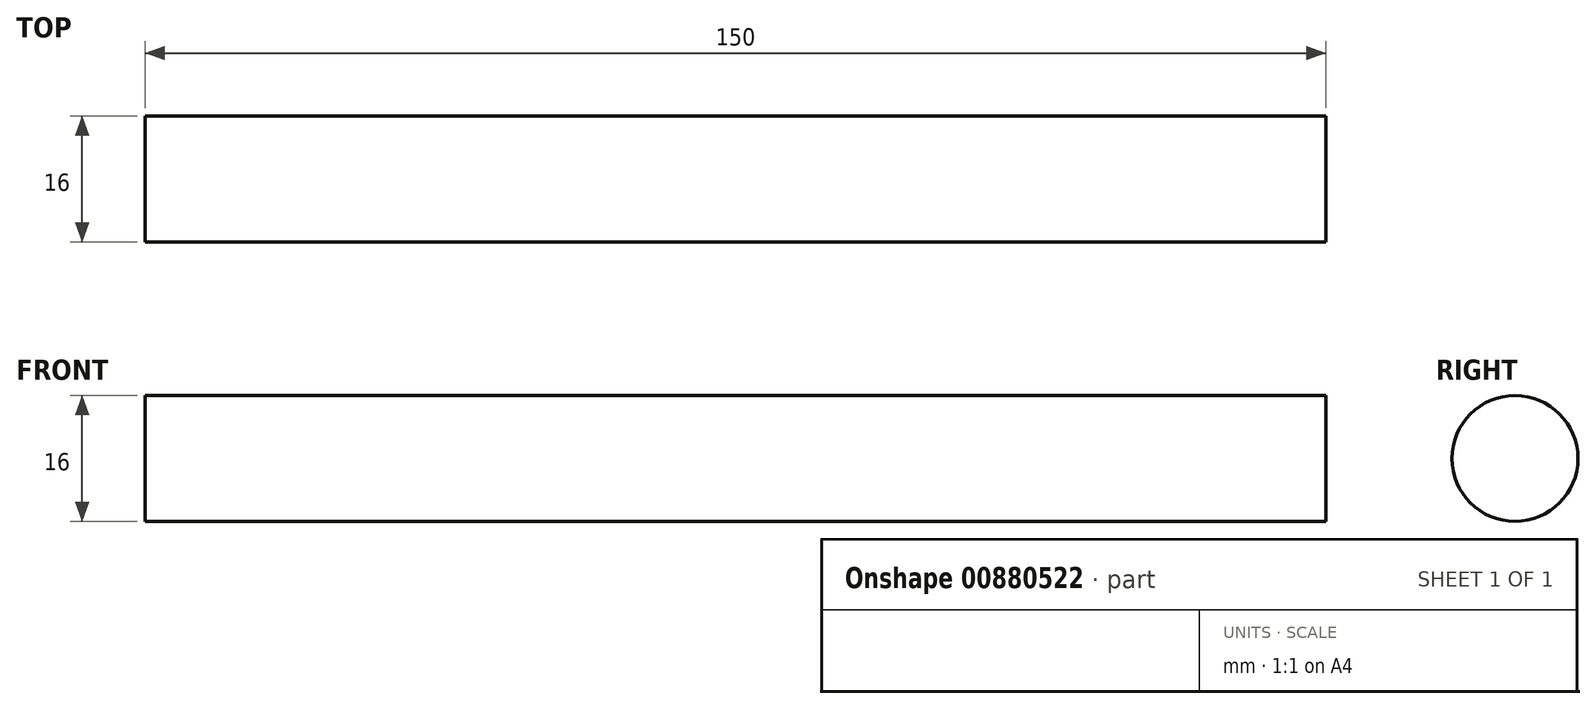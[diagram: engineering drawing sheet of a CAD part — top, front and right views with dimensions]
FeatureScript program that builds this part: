
annotation { "Feature Type Name" : "Feature", "Feature Type Description" : "" }
export const myFeature = defineFeature(function(context is Context, id is Id, definition is map)
    precondition{}
    {
        {
            var Q0;
            Q0=qCreatedBy(makeId("Right.planeOp"),FACE);
            var sketch = newSketch(context, id + "F0", { "sketchPlane" : qUnion([Q0])});
            skCircle(sketch, "E0", {"center": v(0, 0) * mm, "radius": 8 * mm});
            skSolve(sketch);
        }
        {
            var Q0;
            Q0 = qSketchRegion(id + "F0", true);
            extrude(context, id + "F1", {"entities" : qUnion([Q0]), "depth" : 150 * mm, "offsetDistance" : 25 * mm});
        }
    });
